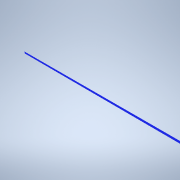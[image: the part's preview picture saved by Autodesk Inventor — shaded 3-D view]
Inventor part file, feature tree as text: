
AUTODESK INVENTOR PART (.ipt)
format: ipt  version: 2020.3 (Build 243373000, 373)  size: 981,504 bytes
history: native  units: mm (DEFAULTED — no unit token found)
features: extrude x2, sketch x2, pattern_linear x1
ambient origin geometry x8: Origin, YZ Plane, XZ Plane, XY Plane, X Axis, Y Axis, Z Axis, Center Point
bodies: Solid1 (feature_tree)
feature tree (5):
  extrude  "Extrusion1"  Depth=5.0mm TaperAngle=0.0deg
  extrude  "Extrusion2"  [1 undecoded]
  pattern_linear  "Rectangular Pattern1"  [2 undecoded]
  sketch  "Sketch_1"  dims[d0=1000.0mm d1=0.0mm d2=5.0mm d3=0.0mm]
  sketch  "Sketch_5"  dims[d4=6410.0mm d6=3.14159mm d7=10.0mm d9=0.0mm]
note: 3 required parameter values undecoded (feature->parameter linkage not recoverable at this tier; creation-order binding heuristic only, values carry confidence <= 0.55)
